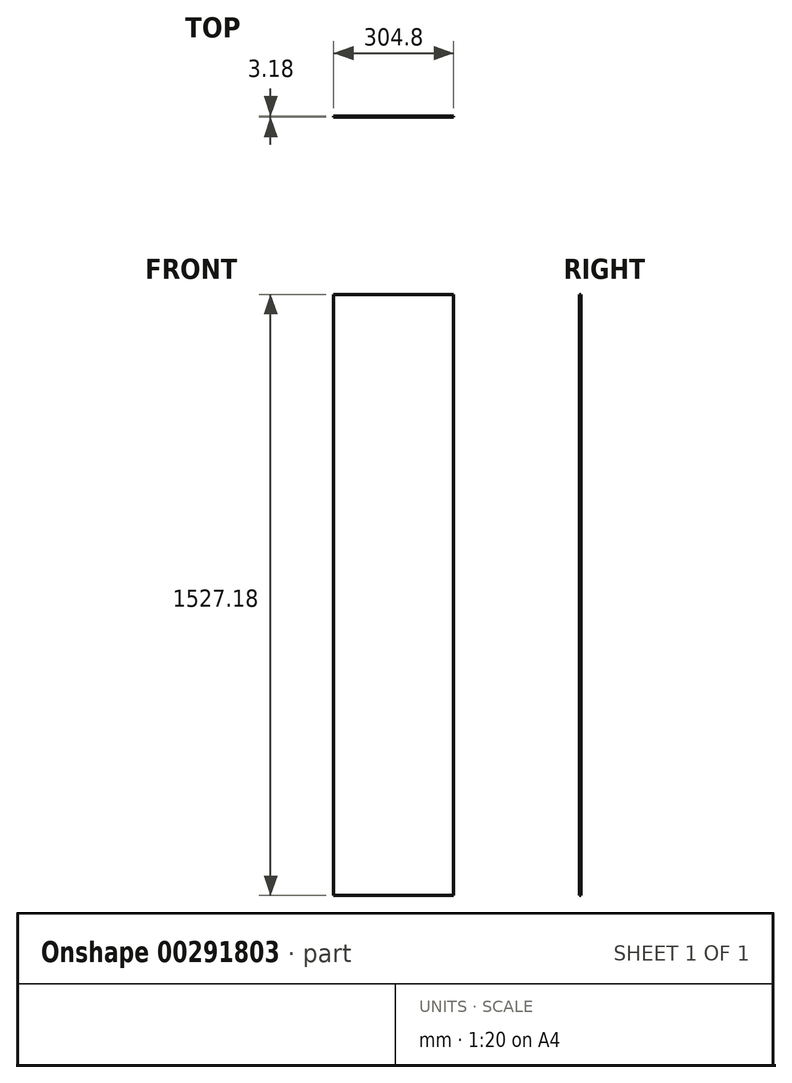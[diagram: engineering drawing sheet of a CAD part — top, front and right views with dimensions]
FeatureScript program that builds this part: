
annotation { "Feature Type Name" : "Feature", "Feature Type Description" : "" }
export const myFeature = defineFeature(function(context is Context, id is Id, definition is map)
    precondition{}
    {
        {
            var Q0;
            Q0=qCreatedBy(makeId("Front.planeOp"),FACE);
            var sketch = newSketch(context, id + "F0", { "sketchPlane" : qUnion([Q0])});
            skLineSegment(sketch, "E0.bottom", {"start": v(152.4, 763.59) * mm, "end": v(-152.4, 763.59) * mm});
            skLineSegment(sketch, "E0.top", {"start": v(152.4, -763.59) * mm, "end": v(-152.4, -763.59) * mm});
            skLineSegment(sketch, "E0.left", {"start": v(152.4, 763.59) * mm, "end": v(152.4, -763.59) * mm});
            skLineSegment(sketch, "E0.right", {"start": v(-152.4, 763.59) * mm, "end": v(-152.4, -763.59) * mm});
            skPoint(sketch, "E0.middle", {"position": v(0, 0) * mm});
            skSolve(sketch);
        }
        {
            var Q0;
            Q0 = qSketchRegion(id + "F0", true);
            extrude(context, id + "F1", {"entities" : qUnion([Q0]), "endBound" : BoundingType.SYMMETRIC, "depth" : 3.17 * mm});
        }
    });
